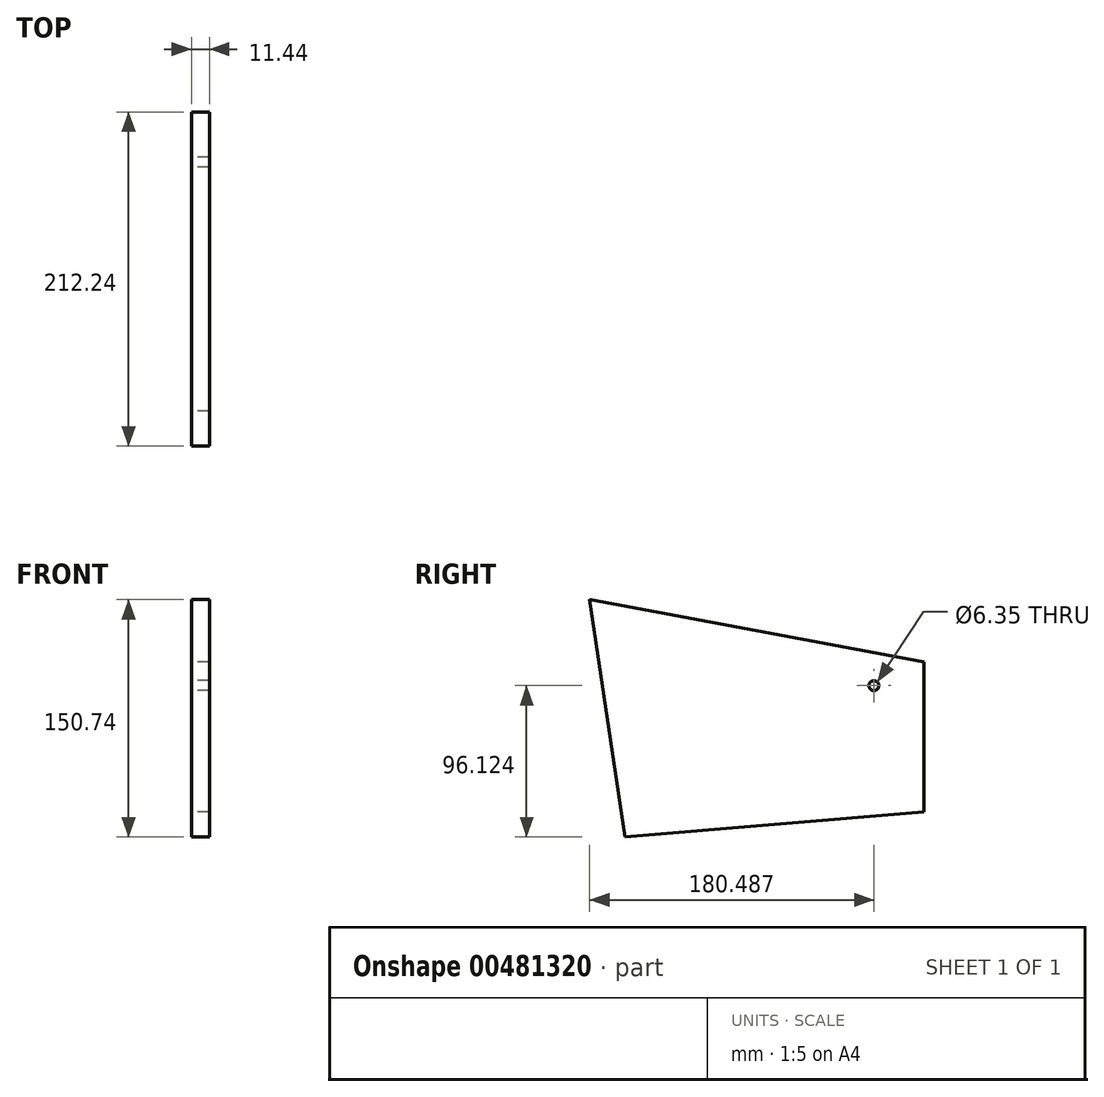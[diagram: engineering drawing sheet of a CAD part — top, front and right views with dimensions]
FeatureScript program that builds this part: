
annotation { "Feature Type Name" : "Feature", "Feature Type Description" : "" }
export const myFeature = defineFeature(function(context is Context, id is Id, definition is map)
    precondition{}
    {
        {
            var Q0;
            Q0=qCreatedBy(makeId("Right.planeOp"),FACE);
            var sketch = newSketch(context, id + "F0", { "sketchPlane" : qUnion([Q0])});
            skLineSegment(sketch, "E0", {"start": v(122.12, 51.37) * mm, "end": v(-90.12, 90.98) * mm});
            skLineSegment(sketch, "E1", {"start": v(-90.12, 90.98) * mm, "end": v(-67.72, -59.76) * mm});
            skLineSegment(sketch, "E2", {"start": v(122.12, 51.37) * mm, "end": v(122.12, -43.88) * mm});
            skLineSegment(sketch, "E3", {"start": v(-67.72, -59.76) * mm, "end": v(122.12, -43.88) * mm});
            skCircle(sketch, "E4", {"center": v(90.37, 36.36) * mm, "radius": 3.18 * mm});
            skCircle(sketch, "E5", {"center": v(109.92, 20.05) * mm, "radius": 3.18 * mm});
            skCircle(sketch, "E6", {"center": v(109.92, -34.05) * mm, "radius": 3.18 * mm});
            skSolve(sketch);
        }
        {
            var Q0;
            Q0=qSketchRegion(id+"F0",true);
            var Q1;
            Q1=makeQuery(id+"F0.imprint","IMPRINT",FACE,{"disambiguationData":[TD([[makeQuery(id+"F0.imprint","IMPRINT",EDGE,{"derivedFrom":sQuery(id+"F0.wireOp",EDGE,"E4")}),1.0]])]});
            var Q2;
            Q2=makeQuery(id+"F0.imprint","IMPRINT",FACE,{"disambiguationData":[TD([[makeQuery(id+"F0.imprint","IMPRINT",EDGE,{"derivedFrom":sQuery(id+"F0.wireOp",EDGE,"E5")}),1.0]])]});
            var Q3;
            Q3=makeQuery(id+"F0.imprint","IMPRINT",FACE,{"disambiguationData":[TD([[makeQuery(id+"F0.imprint","IMPRINT",EDGE,{"derivedFrom":sQuery(id+"F0.wireOp",EDGE,"E6")}),1.0]])]});
            extrude(context, id + "F1", {"entities" : qUnion([Q0, Q1, Q2, Q3]), "depth" : 11.43 * mm});
        }
        {
            var Q0;
            Q0=makeQuery(id+"F1.opExtrude","SWEPT_BODY",BODY,{"disambiguationData":[OSD([sQuery(id+"F0.wireOp",EDGE,"E0"),sQuery(id+"F0.wireOp",EDGE,"E1"),sQuery(id+"F0.wireOp",EDGE,"E2"),sQuery(id+"F0.wireOp",EDGE,"E3"),sQuery(id+"F0.wireOp",EDGE,"E4"),sQuery(id+"F0.wireOp",EDGE,"E5"),sQuery(id+"F0.wireOp",EDGE,"E6")])]});
            transform(context, id + "F2", {"entities" : qUnion([Q0]), "transformType" : TransformType.TRANSLATION_3D, "dx" : 47.62 * mm, "dy" : 0 * mm, "dz" : 0 * mm, "makeCopy" : false});
        }
        {
            var Q0;
            Q0=makeQuery(id+"F1.opExtrude","SWEPT_BODY",BODY,{"disambiguationData":[OSD([sQuery(id+"F0.wireOp",EDGE,"E0"),sQuery(id+"F0.wireOp",EDGE,"E1"),sQuery(id+"F0.wireOp",EDGE,"E2"),sQuery(id+"F0.wireOp",EDGE,"E3"),sQuery(id+"F0.wireOp",EDGE,"E4"),sQuery(id+"F0.wireOp",EDGE,"E5"),sQuery(id+"F0.wireOp",EDGE,"E6")])]});
            var Q1;
            Q1=qCreatedBy(makeId("Right.planeOp"),FACE);
            mirror(context, id + "F3", {"entities" : qUnion([Q0]), "mirrorPlane" : qUnion([Q1])});
        }
        {
            var Q0;
            Q0=makeQuery(id+"F3.opPattern","COPY",FACE,{"derivedFrom":makeQuery(id+"F1.opExtrude","CAP_FACE",FACE,{"disambiguationData":[OSD([sQuery(id+"F0.wireOp",EDGE,"E0"),sQuery(id+"F0.wireOp",EDGE,"E1"),sQuery(id+"F0.wireOp",EDGE,"E2"),sQuery(id+"F0.wireOp",EDGE,"E3"),sQuery(id+"F0.wireOp",EDGE,"E4"),sQuery(id+"F0.wireOp",EDGE,"E5"),sQuery(id+"F0.wireOp",EDGE,"E6")])],"isStart":false}),"instanceName":"1"});
            var sketch = newSketch(context, id + "F4", { "sketchPlane" : qUnion([Q0])});
            skLineSegment(sketch, "E7", {"start": v(-122.12, -43.88) * mm, "end": v(-33.22, -43.88) * mm});
            skCircle(sketch, "E8", {"center": v(-33.22, -43.88) * mm, "radius": 50.8 * mm});
            skLineSegment(sketch, "E9", {"start": v(17.58, -43.88) * mm, "end": v(17.58, -55.57) * mm});
            skSolve(sketch);
        }
        {
            var Q0;
            {var subQ0=sQuery(id+"F4.wireOp",EDGE,"E8");var subQ1=makeQuery(id+"F4.imprint","INTERSECT",VERTEX,{"derivedFrom":[subQ0,sQuery(id+"F4.wireOp",EDGE,"E9")]});Q0=makeQuery(id+"F4.imprint","IMPRINT",FACE,{"disambiguationData":[TD([[makeQuery(id+"F4.imprint","IMPRINT",EDGE,{"disambiguationData":[TD([[subQ1,-1.0]])],"derivedFrom":subQ0}),1.0]])]});}
            var Q1;
            {var subQ0=sQuery(id+"F4.wireOp",EDGE,"E9");Q1=makeQuery(id+"F4.imprint","IMPRINT",FACE,{"disambiguationData":[TD([[makeQuery(id+"F4.imprint","IMPRINT",EDGE,{"derivedFrom":subQ0}),-1.0]])]});}
            extrude(context, id + "F5", {"entities" : qUnion([Q0, Q1]), "operationType" : NewBodyOperationType.REMOVE, "oppositeDirection" : true, "depth" : 25.4 * mm});
        }
        {
            var Q0;
            Q0=sQuery(id+"F0.wireOp",VERTEX,"E4.center");
            var Q1;
            Q1=makeQuery(id+"F3.opPattern","COPY",BODY,{"derivedFrom":makeQuery(id+"F1.opExtrude","SWEPT_BODY",BODY,{"disambiguationData":[OSD([sQuery(id+"F0.wireOp",EDGE,"E0"),sQuery(id+"F0.wireOp",EDGE,"E1"),sQuery(id+"F0.wireOp",EDGE,"E2"),sQuery(id+"F0.wireOp",EDGE,"E3")])]}),"instanceName":"1"});
            hole(context, id + "F6", {"style" : HoleStyle.SIMPLE, "endStyle" : HoleEndStyle.BLIND, "holeDiameter" : 6.35 * mm, "holeDepth" : 76.2 * mm, "isTappedThrough" : true, "tappedDepth" : 12.7 * mm, "tapClearance" : 3, "startFromSketch" : true, "locations" : qUnion([Q0]), "scope" : qUnion([Q1])});
        }
        {
            var Q0;
            Q0=sQuery(id+"F0.wireOp",VERTEX,"E5.center");
            var Q1;
            Q1=makeQuery(id+"F3.opPattern","COPY",BODY,{"derivedFrom":makeQuery(id+"F1.opExtrude","SWEPT_BODY",BODY,{"disambiguationData":[OSD([sQuery(id+"F0.wireOp",EDGE,"E0"),sQuery(id+"F0.wireOp",EDGE,"E1"),sQuery(id+"F0.wireOp",EDGE,"E2"),sQuery(id+"F0.wireOp",EDGE,"E3")])]}),"instanceName":"1"});
            hole(context, id + "F7", {"style" : HoleStyle.SIMPLE, "endStyle" : HoleEndStyle.BLIND, "holeDiameter" : 6.35 * mm, "holeDepth" : 76.2 * mm, "isTappedThrough" : true, "tappedDepth" : 12.7 * mm, "tapClearance" : 3, "startFromSketch" : true, "locations" : qUnion([Q0]), "scope" : qUnion([Q1])});
        }
        {
            var Q0;
            Q0=sQuery(id+"F0.wireOp",VERTEX,"E6.center");
            var Q1;
            Q1=makeQuery(id+"F3.opPattern","COPY",BODY,{"derivedFrom":makeQuery(id+"F1.opExtrude","SWEPT_BODY",BODY,{"disambiguationData":[OSD([sQuery(id+"F0.wireOp",EDGE,"E0"),sQuery(id+"F0.wireOp",EDGE,"E1"),sQuery(id+"F0.wireOp",EDGE,"E2"),sQuery(id+"F0.wireOp",EDGE,"E3")])]}),"instanceName":"1"});
            hole(context, id + "F8", {"style" : HoleStyle.SIMPLE, "endStyle" : HoleEndStyle.BLIND, "holeDiameter" : 6.35 * mm, "holeDepth" : 76.2 * mm, "isTappedThrough" : true, "tappedDepth" : 12.7 * mm, "tapClearance" : 3, "startFromSketch" : true, "locations" : qUnion([Q0]), "scope" : qUnion([Q1])});
        }
        {
            var Q0;
            Q0=sQuery(id+"F0.wireOp",VERTEX,"E4.center");
            var Q1;
            Q1=makeQuery(id+"F1.opExtrude","SWEPT_BODY",BODY,{"disambiguationData":[OSD([sQuery(id+"F0.wireOp",EDGE,"E0"),sQuery(id+"F0.wireOp",EDGE,"E1"),sQuery(id+"F0.wireOp",EDGE,"E2"),sQuery(id+"F0.wireOp",EDGE,"E3")])]});
            hole(context, id + "F9", {"style" : HoleStyle.SIMPLE, "endStyle" : HoleEndStyle.BLIND, "oppositeDirection" : true, "holeDiameter" : 6.35 * mm, "holeDepth" : 76.2 * mm, "isTappedThrough" : true, "tappedDepth" : 12.7 * mm, "tapClearance" : 3, "startFromSketch" : true, "locations" : qUnion([Q0]), "scope" : qUnion([Q1])});
        }
        {
            var Q0;
            Q0=makeQuery(id+"F1.opExtrude","CAP_FACE",FACE,{"disambiguationData":[OSD([sQuery(id+"F0.wireOp",EDGE,"E0"),sQuery(id+"F0.wireOp",EDGE,"E1"),sQuery(id+"F0.wireOp",EDGE,"E2"),sQuery(id+"F0.wireOp",EDGE,"E3")])],"isStart":true});
            var sketch = newSketch(context, id + "F10", { "sketchPlane" : qUnion([Q0])});
            skCircle(sketch, "E10", {"center": v(-90.37, 36.36) * mm, "radius": 66.68 * mm});
            skCircle(sketch, "E11.0", {"center": v(-90.37, 36.36) * mm, "radius": 161.93 * mm});
            skCircle(sketch, "E12.0", {"center": v(-90.37, 36.36) * mm, "radius": 164.47 * mm});
            skLineSegment(sketch, "E13", {"start": v(52.96, -38.98) * mm, "end": v(55.23, -40.13) * mm});
            skLineSegment(sketch, "E14", {"start": v(66.26, 86.53) * mm, "end": v(48.44, 142.17) * mm});
            skLineSegment(sketch, "E15", {"start": v(48.44, 142.17) * mm, "end": v(46.02, 141.4) * mm});
            skLineSegment(sketch, "E16", {"start": v(46.02, 141.4) * mm, "end": v(63.74, 86.06) * mm});
            skSolve(sketch);
        }
        {
            var Q0;
            {var subQ0=sQuery(id+"F10.wireOp",EDGE,"E14");Q0=makeQuery(id+"F10.imprint","IMPRINT",FACE,{"disambiguationData":[TD([[makeQuery(id+"F10.imprint","IMPRINT",EDGE,{"derivedFrom":subQ0}),1.0]])]});}
            var Q1;
            {var subQ1=makeQuery(id+"F1.opExtrude","CAP_EDGE",EDGE,{"disambiguationData":[OSD([sQuery(id+"F0.wireOp",EDGE,"E0")])],"isStart":true});var subQ3=sQuery(id+"F10.wireOp",EDGE,"E16");var subQ5=makeQuery(id+"F10.imprint","INTERSECT",VERTEX,{"derivedFrom":[subQ1,subQ3]});Q1=makeQuery(id+"F10.imprint","IMPRINT",FACE,{"disambiguationData":[TD([[makeQuery(id+"F10.imprint","IMPRINT",EDGE,{"disambiguationData":[TD([[subQ5,1.0]])],"derivedFrom":subQ3}),1.0]])]});}
            var Q2;
            {var subQ4=sQuery(id+"F10.wireOp",EDGE,"E13");Q2=makeQuery(id+"F10.imprint","IMPRINT",FACE,{"disambiguationData":[TD([[makeQuery(id+"F10.imprint","IMPRINT",EDGE,{"derivedFrom":subQ4}),1.0]])]});}
            extrude(context, id + "F11", {"entities" : qUnion([Q0, Q1, Q2]), "depth" : 95.25 * mm});
        }
        {
            var Q0;
            Q0=makeQuery(id+"F3.opPattern","COPY",BODY,{"derivedFrom":makeQuery(id+"F1.opExtrude","SWEPT_BODY",BODY,{"disambiguationData":[OSD([sQuery(id+"F0.wireOp",EDGE,"E0"),sQuery(id+"F0.wireOp",EDGE,"E1"),sQuery(id+"F0.wireOp",EDGE,"E2"),sQuery(id+"F0.wireOp",EDGE,"E3")])]}),"instanceName":"1"});
            deleteBodies(context, id + "F12", {"entities" : qUnion([Q0])});
        }
        {
            var Q0;
            Q0=makeQuery(id+"F11.opExtrude","SWEPT_BODY",BODY,{"disambiguationData":[OSD([sQuery(id+"F0.wireOp",EDGE,"E0"),sQuery(id+"F10.wireOp",EDGE,"E11.0"),sQuery(id+"F10.wireOp",EDGE,"E12.0"),sQuery(id+"F10.wireOp",EDGE,"E13"),sQuery(id+"F10.wireOp",EDGE,"E14"),sQuery(id+"F10.wireOp",EDGE,"E15"),sQuery(id+"F10.wireOp",EDGE,"E16")])]});
            deleteBodies(context, id + "F13", {"entities" : qUnion([Q0])});
        }
    });
